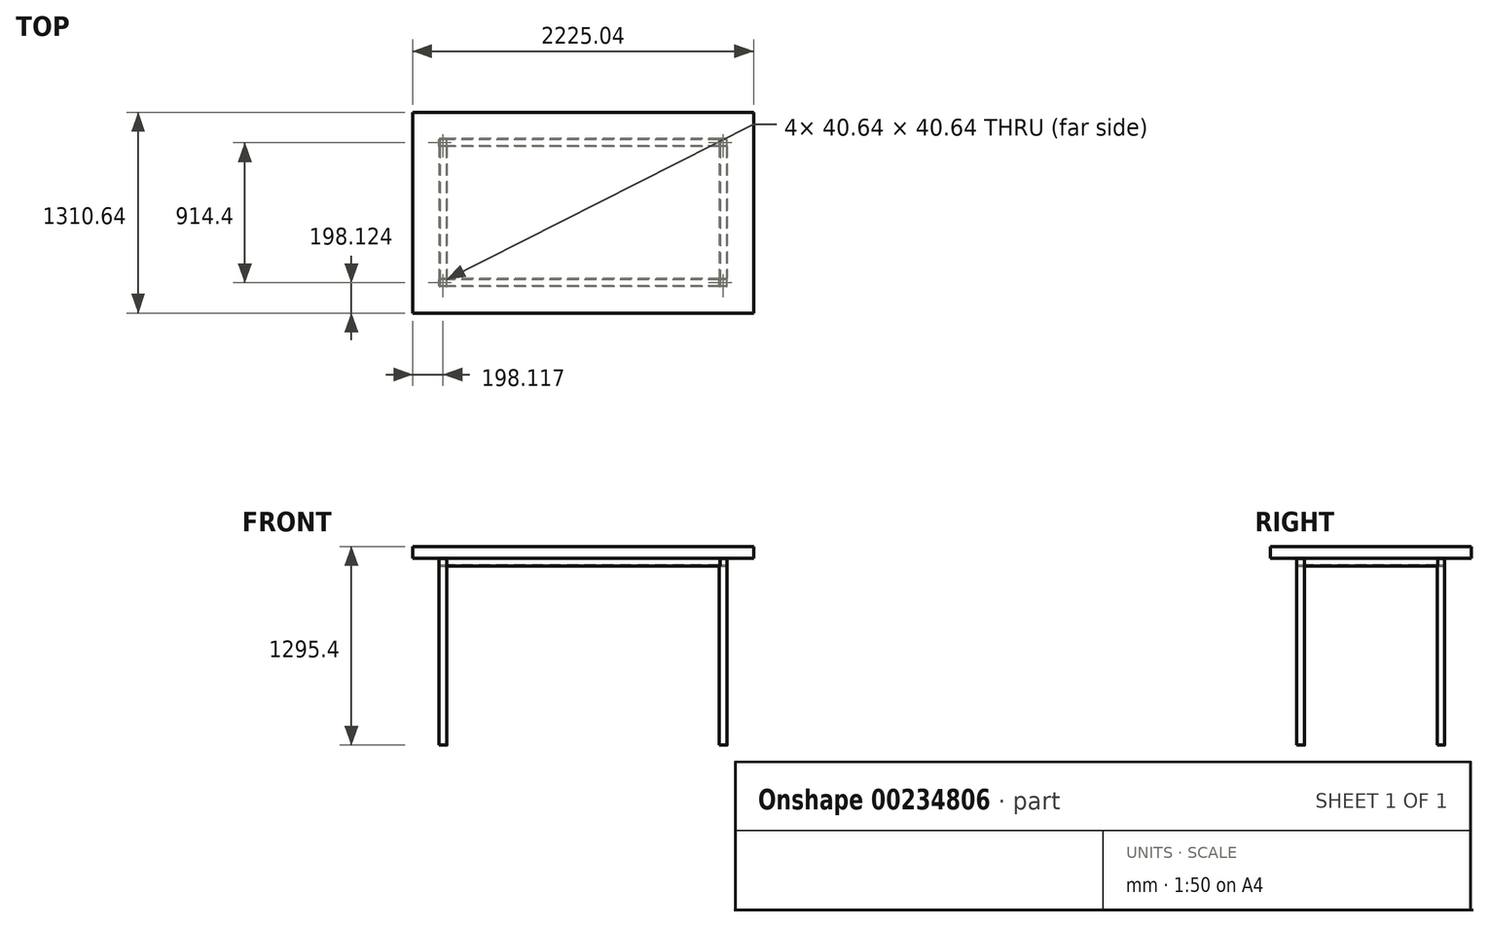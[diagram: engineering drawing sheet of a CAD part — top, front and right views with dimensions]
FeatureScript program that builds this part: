
annotation { "Feature Type Name" : "Feature", "Feature Type Description" : "" }
export const myFeature = defineFeature(function(context is Context, id is Id, definition is map)
    precondition{}
    {
        {
            var Q0;
            Q0=qCreatedBy(makeId("Top.planeOp"),FACE);
            var sketch = newSketch(context, id + "F0", { "sketchPlane" : qUnion([Q0])});
            skLineSegment(sketch, "E0.bottom", {"start": v(-38.46, 16.77) * mm, "end": v(-89.26, 16.77) * mm});
            skLineSegment(sketch, "E0.top", {"start": v(-38.46, 67.57) * mm, "end": v(-89.26, 67.57) * mm});
            skLineSegment(sketch, "E0.left", {"start": v(-38.46, 16.77) * mm, "end": v(-38.46, 67.57) * mm});
            skLineSegment(sketch, "E0.right", {"start": v(-89.26, 16.77) * mm, "end": v(-89.26, 67.57) * mm});
            skPoint(sketch, "E0.middle", {"position": v(-63.86, 42.17) * mm});
            skLineSegment(sketch, "E1.bottom", {"start": v(-43.54, 62.5) * mm, "end": v(-84.18, 62.5) * mm});
            skLineSegment(sketch, "E1.top", {"start": v(-43.54, 21.85) * mm, "end": v(-84.18, 21.85) * mm});
            skLineSegment(sketch, "E1.left", {"start": v(-43.54, 62.5) * mm, "end": v(-43.54, 21.85) * mm});
            skLineSegment(sketch, "E1.right", {"start": v(-84.18, 62.5) * mm, "end": v(-84.18, 21.85) * mm});
            skSolve(sketch);
        }
        {
            var Q0;
            Q0 = qSketchRegion(id + "F0", true);
            extrude(context, id + "F1", {"entities" : qUnion([Q0]), "oppositeDirection" : true, "offsetDistance" : 25 * mm, "depth" : 1219.2 * mm});
        }
        {
            var Q0;
            Q0=makeQuery(id+"F1.opExtrude","SWEPT_EDGE",EDGE,{"disambiguationData":[OSD([sQuery(id+"F0.wireOp",EDGE,"E0.bottom"),sQuery(id+"F0.wireOp",EDGE,"E0.right")])]});
            var Q1;
            Q1=makeQuery(id+"F1.opExtrude","SWEPT_EDGE",EDGE,{"disambiguationData":[OSD([sQuery(id+"F0.wireOp",EDGE,"E0.top"),sQuery(id+"F0.wireOp",EDGE,"E0.right")])]});
            var Q2;
            Q2=makeQuery(id+"F1.opExtrude","SWEPT_EDGE",EDGE,{"disambiguationData":[OSD([sQuery(id+"F0.wireOp",EDGE,"E0.bottom"),sQuery(id+"F0.wireOp",EDGE,"E0.left")])]});
            var Q3;
            Q3=makeQuery(id+"F1.opExtrude","SWEPT_EDGE",EDGE,{"disambiguationData":[OSD([sQuery(id+"F0.wireOp",EDGE,"E0.top"),sQuery(id+"F0.wireOp",EDGE,"E0.left")])]});
            fillet(context, id + "F2", {"entities" : qUnion([Q0, Q1, Q2, Q3]), "radius" : 5.08 * mm, "tangentPropagation" : true, "allowEdgeOverflow" : false});
        }
        {
            var Q0;
            Q0=makeQuery(id+"F1.opExtrude","SWEPT_BODY",BODY,{"disambiguationData":[OSD([sQuery(id+"F0.wireOp",EDGE,"E0.bottom"),sQuery(id+"F0.wireOp",EDGE,"E0.top"),sQuery(id+"F0.wireOp",EDGE,"E0.left"),sQuery(id+"F0.wireOp",EDGE,"E0.right"),sQuery(id+"F0.wireOp",EDGE,"E1.bottom"),sQuery(id+"F0.wireOp",EDGE,"E1.top"),sQuery(id+"F0.wireOp",EDGE,"E1.left"),sQuery(id+"F0.wireOp",EDGE,"E1.right")])]});
            transform(context, id + "F3", {"entities" : qUnion([Q0]), "transformType" : TransformType.TRANSLATION_3D, "dx" : 1828.8 * mm, "dy" : 0 * mm, "dz" : 0 * mm, "makeCopy" : true});
        }
        {
            var Q0;
            Q0=makeQuery(id+"F1.opExtrude","SWEPT_BODY",BODY,{"disambiguationData":[OSD([sQuery(id+"F0.wireOp",EDGE,"E0.bottom"),sQuery(id+"F0.wireOp",EDGE,"E0.top"),sQuery(id+"F0.wireOp",EDGE,"E0.left"),sQuery(id+"F0.wireOp",EDGE,"E0.right"),sQuery(id+"F0.wireOp",EDGE,"E1.bottom"),sQuery(id+"F0.wireOp",EDGE,"E1.top"),sQuery(id+"F0.wireOp",EDGE,"E1.left"),sQuery(id+"F0.wireOp",EDGE,"E1.right")])]});
            transform(context, id + "F4", {"entities" : qUnion([Q0]), "transformType" : TransformType.TRANSLATION_3D, "dx" : 0 * mm, "dy" : 914.4 * mm, "dz" : 0 * mm, "makeCopy" : true});
        }
        {
            var Q0;
            Q0=makeQuery(id+"F4.opPattern","COPY",BODY,{"derivedFrom":makeQuery(id+"F1.opExtrude","SWEPT_BODY",BODY,{"disambiguationData":[OSD([sQuery(id+"F0.wireOp",EDGE,"E0.bottom"),sQuery(id+"F0.wireOp",EDGE,"E0.top"),sQuery(id+"F0.wireOp",EDGE,"E0.left"),sQuery(id+"F0.wireOp",EDGE,"E0.right"),sQuery(id+"F0.wireOp",EDGE,"E1.bottom"),sQuery(id+"F0.wireOp",EDGE,"E1.top"),sQuery(id+"F0.wireOp",EDGE,"E1.left"),sQuery(id+"F0.wireOp",EDGE,"E1.right")])]}),"instanceName":"1"});
            transform(context, id + "F5", {"entities" : qUnion([Q0]), "transformType" : TransformType.TRANSLATION_3D, "dx" : 1828.8 * mm, "dy" : 0 * mm, "dz" : 0 * mm, "makeCopy" : true});
        }
        {
            var Q0;
            Q0=makeQuery(id+"F1.opExtrude","SWEPT_FACE",FACE,{"disambiguationData":[OSD([sQuery(id+"F0.wireOp",EDGE,"E0.left")])]});
            var sketch = newSketch(context, id + "F6", { "sketchPlane" : qUnion([Q0])});
            skLineSegment(sketch, "E2.bottom", {"start": v(16.77, 0) * mm, "end": v(67.57, 0) * mm});
            skLineSegment(sketch, "E2.top", {"start": v(16.77, -50.8) * mm, "end": v(67.57, -50.8) * mm});
            skLineSegment(sketch, "E2.left", {"start": v(16.77, 0) * mm, "end": v(16.77, -50.8) * mm});
            skLineSegment(sketch, "E2.right", {"start": v(67.57, 0) * mm, "end": v(67.57, -50.8) * mm});
            skLineSegment(sketch, "E3.bottom", {"start": v(21.85, -5.08) * mm, "end": v(62.5, -5.08) * mm});
            skLineSegment(sketch, "E3.top", {"start": v(21.85, -45.72) * mm, "end": v(62.5, -45.72) * mm});
            skLineSegment(sketch, "E3.left", {"start": v(21.85, -5.08) * mm, "end": v(21.85, -45.72) * mm});
            skLineSegment(sketch, "E3.right", {"start": v(62.5, -5.08) * mm, "end": v(62.5, -45.72) * mm});
            skSolve(sketch);
        }
        {
            var Q0;
            Q0 = qSketchRegion(id + "F6", true);
            var Q1;
            Q1=makeQuery(id+"F3.opPattern","COPY",BODY,{"derivedFrom":makeQuery(id+"F1.opExtrude","SWEPT_BODY",BODY,{"disambiguationData":[OSD([sQuery(id+"F0.wireOp",EDGE,"E0.bottom"),sQuery(id+"F0.wireOp",EDGE,"E0.top"),sQuery(id+"F0.wireOp",EDGE,"E0.left"),sQuery(id+"F0.wireOp",EDGE,"E0.right"),sQuery(id+"F0.wireOp",EDGE,"E1.bottom"),sQuery(id+"F0.wireOp",EDGE,"E1.top"),sQuery(id+"F0.wireOp",EDGE,"E1.left"),sQuery(id+"F0.wireOp",EDGE,"E1.right")])]}),"instanceName":"1"});
            extrude(context, id + "F7", {"entities" : qUnion([Q0]), "endBound" : BoundingType.UP_TO_BODY, "endBoundEntityBody" : qUnion([Q1]), "depth" : 508 * mm});
        }
        {
            var Q0;
            Q0=makeQuery(id+"F7.opExtrude","SWEPT_EDGE",EDGE,{"disambiguationData":[OSD([sQuery(id+"F6.wireOp",EDGE,"E2.bottom"),sQuery(id+"F6.wireOp",EDGE,"E2.right")])]});
            var Q1;
            Q1=makeQuery(id+"F7.opExtrude","SWEPT_EDGE",EDGE,{"disambiguationData":[OSD([sQuery(id+"F0.wireOp",EDGE,"E0.bottom"),sQuery(id+"F0.wireOp",EDGE,"E0.top"),sQuery(id+"F0.wireOp",EDGE,"E0.left"),sQuery(id+"F0.wireOp",EDGE,"E0.right"),sQuery(id+"F0.wireOp",EDGE,"E1.bottom"),sQuery(id+"F0.wireOp",EDGE,"E1.top"),sQuery(id+"F0.wireOp",EDGE,"E1.left"),sQuery(id+"F0.wireOp",EDGE,"E1.right")])]});
            var Q2;
            Q2=makeQuery(id+"F7.opExtrude","SWEPT_EDGE",EDGE,{"disambiguationData":[OSD([sQuery(id+"F6.wireOp",EDGE,"E2.top"),sQuery(id+"F6.wireOp",EDGE,"E2.right")])]});
            var Q3;
            Q3=makeQuery(id+"F7.opExtrude","SWEPT_EDGE",EDGE,{"disambiguationData":[OSD([sQuery(id+"F6.wireOp",EDGE,"E2.top"),sQuery(id+"F6.wireOp",EDGE,"E2.left")])]});
            fillet(context, id + "F8", {"entities" : qUnion([Q0, Q1, Q2, Q3]), "radius" : 5.08 * mm, "tangentPropagation" : true, "allowEdgeOverflow" : false});
        }
        {
            var Q0;
            Q0=makeQuery(id+"F7.opExtrude","SWEPT_BODY",BODY,{"disambiguationData":[OSD([sQuery(id+"F6.wireOp",EDGE,"E2.bottom"),sQuery(id+"F6.wireOp",EDGE,"E2.top"),sQuery(id+"F6.wireOp",EDGE,"E2.left"),sQuery(id+"F6.wireOp",EDGE,"E2.right"),sQuery(id+"F6.wireOp",EDGE,"E3.bottom"),sQuery(id+"F6.wireOp",EDGE,"E3.top"),sQuery(id+"F6.wireOp",EDGE,"E3.left"),sQuery(id+"F6.wireOp",EDGE,"E3.right")])]});
            transform(context, id + "F9", {"entities" : qUnion([Q0]), "transformType" : TransformType.TRANSLATION_3D, "dx" : 0 * mm, "dy" : 914.4 * mm, "dz" : 0 * mm, "makeCopy" : true});
        }
        {
            var Q0;
            Q0=makeQuery(id+"F1.opExtrude","SWEPT_FACE",FACE,{"disambiguationData":[OSD([sQuery(id+"F0.wireOp",EDGE,"E0.top")])]});
            var sketch = newSketch(context, id + "F10", { "sketchPlane" : qUnion([Q0])});
            skLineSegment(sketch, "E4.bottom", {"start": v(89.26, -50.8) * mm, "end": v(38.46, -50.8) * mm});
            skLineSegment(sketch, "E4.top", {"start": v(89.26, 0) * mm, "end": v(38.46, 0) * mm});
            skLineSegment(sketch, "E4.left", {"start": v(89.26, -50.8) * mm, "end": v(89.26, 0) * mm});
            skLineSegment(sketch, "E4.right", {"start": v(38.46, -50.8) * mm, "end": v(38.46, 0) * mm});
            skLineSegment(sketch, "E5.bottom", {"start": v(84.18, -45.72) * mm, "end": v(43.54, -45.72) * mm});
            skLineSegment(sketch, "E5.top", {"start": v(84.18, -5.08) * mm, "end": v(43.54, -5.08) * mm});
            skLineSegment(sketch, "E5.left", {"start": v(84.18, -45.72) * mm, "end": v(84.18, -5.08) * mm});
            skLineSegment(sketch, "E5.right", {"start": v(43.54, -45.72) * mm, "end": v(43.54, -5.08) * mm});
            skSolve(sketch);
        }
        {
            var Q0;
            Q0 = qSketchRegion(id + "F10", true);
            extrude(context, id + "F11", {"entities" : qUnion([Q0]), "endBound" : BoundingType.UP_TO_NEXT, "depth" : 25.4 * mm});
        }
        {
            var Q0;
            Q0=makeQuery(id+"F11.opExtrude","SWEPT_EDGE",EDGE,{"disambiguationData":[OSD([sQuery(id+"F10.wireOp",EDGE,"E4.bottom"),sQuery(id+"F10.wireOp",EDGE,"E4.left")])]});
            var Q1;
            Q1=makeQuery(id+"F11.opExtrude","SWEPT_EDGE",EDGE,{"disambiguationData":[OSD([sQuery(id+"F10.wireOp",EDGE,"E4.bottom"),sQuery(id+"F10.wireOp",EDGE,"E4.right")])]});
            var Q2;
            Q2=makeQuery(id+"F11.opExtrude","SWEPT_EDGE",EDGE,{"disambiguationData":[OSD([sQuery(id+"F10.wireOp",EDGE,"E4.top"),sQuery(id+"F10.wireOp",EDGE,"E4.left")])]});
            var Q3;
            Q3=makeQuery(id+"F11.opExtrude","SWEPT_EDGE",EDGE,{"disambiguationData":[OSD([sQuery(id+"F10.wireOp",EDGE,"E4.top"),sQuery(id+"F10.wireOp",EDGE,"E4.right")])]});
            fillet(context, id + "F12", {"entities" : qUnion([Q0, Q1, Q2, Q3]), "radius" : 5.08 * mm, "tangentPropagation" : true, "allowEdgeOverflow" : false});
        }
        {
            var Q0;
            Q0=makeQuery(id+"F11.opExtrude","SWEPT_BODY",BODY,{"disambiguationData":[OSD([sQuery(id+"F10.wireOp",EDGE,"E4.bottom"),sQuery(id+"F10.wireOp",EDGE,"E4.top"),sQuery(id+"F10.wireOp",EDGE,"E4.left"),sQuery(id+"F10.wireOp",EDGE,"E4.right"),sQuery(id+"F10.wireOp",EDGE,"E5.bottom"),sQuery(id+"F10.wireOp",EDGE,"E5.top"),sQuery(id+"F10.wireOp",EDGE,"E5.left"),sQuery(id+"F10.wireOp",EDGE,"E5.right")])]});
            transform(context, id + "F13", {"entities" : qUnion([Q0]), "transformType" : TransformType.TRANSLATION_3D, "dx" : 1828.8 * mm, "dy" : 0 * mm, "dz" : 0 * mm, "makeCopy" : true});
        }
        {
            var Q0;
            Q0=makeQuery(id+"F9.opPattern","COPY",FACE,{"derivedFrom":makeQuery(id+"F7.opExtrude","SWEPT_FACE",FACE,{"disambiguationData":[OSD([sQuery(id+"F6.wireOp",EDGE,"E2.bottom")])]}),"instanceName":"1"});
            var sketch = newSketch(context, id + "F14", { "sketchPlane" : qUnion([Q0])});
            skLineSegment(sketch, "E6.bottom", {"start": v(-261.98, 1154.7) * mm, "end": v(1963.06, 1154.7) * mm});
            skLineSegment(sketch, "E6.top", {"start": v(-261.98, -155.95) * mm, "end": v(1963.06, -155.95) * mm});
            skLineSegment(sketch, "E6.left", {"start": v(-261.98, 1154.7) * mm, "end": v(-261.98, -155.95) * mm});
            skLineSegment(sketch, "E6.right", {"start": v(1963.06, 1154.7) * mm, "end": v(1963.06, -155.95) * mm});
            skSolve(sketch);
        }
        {
            var Q0;
            Q0 = qSketchRegion(id + "F14", true);
            extrude(context, id + "F15", {"entities" : qUnion([Q0]), "depth" : 76.2 * mm, "offsetDistance" : 25.4 * mm});
        }
    });
